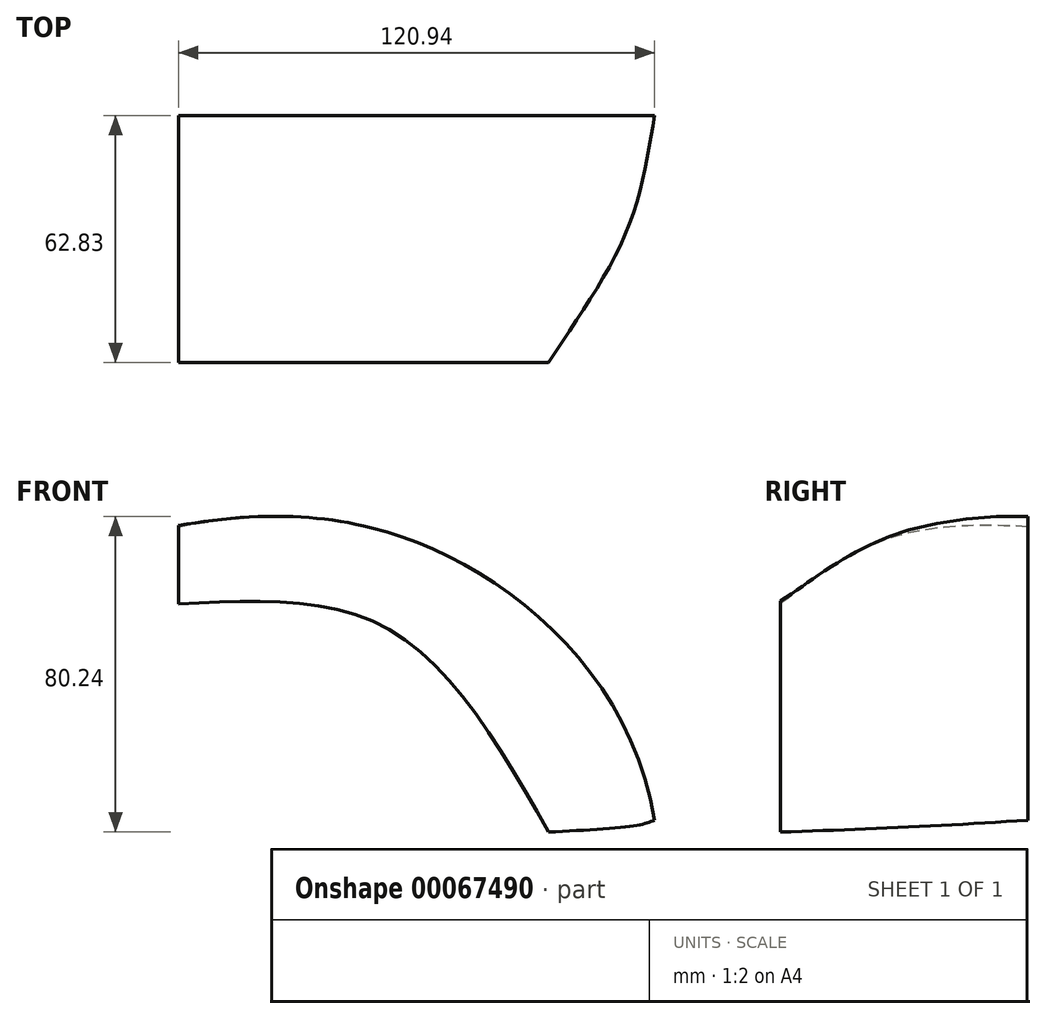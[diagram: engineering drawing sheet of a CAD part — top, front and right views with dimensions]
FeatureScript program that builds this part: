
annotation { "Feature Type Name" : "Feature", "Feature Type Description" : "" }
export const myFeature = defineFeature(function(context is Context, id is Id, definition is map)
    precondition{}
    {
        {
            var Q0;
            Q0=qCreatedBy(makeId("Right.planeOp"),FACE);
            cPlane(context, id + "F0", {"entities" : qUnion([Q0]), "cplaneType" : CPlaneType.OFFSET, "offset" : 140 * mm, "oppositeDirection" : true, "width" : 150 * mm, "height" : 150 * mm});
        }
        {
            var Q0;
            Q0=qCreatedBy(makeId("Right.planeOp"),FACE);
            cPlane(context, id + "F1", {"entities" : qUnion([Q0]), "cplaneType" : CPlaneType.OFFSET, "offset" : 95 * mm, "width" : 150 * mm, "height" : 150 * mm});
        }
        {
            var Q0;
            Q0=qCreatedBy(makeId("Front.planeOp"),FACE);
            var sketch = newSketch(context, id + "F2", { "sketchPlane" : qUnion([Q0])});
            skFitSpline(sketch, "E0", {"points": [v(-26.82, 108.95) * mm, v(37.57, 103.37) * mm, v(94.12, 34.37) * mm], "startDerivative": vector(145.94, 27.93) * mm, "endDerivative": vector(31.71, -191.73) * mm});
            skSolve(sketch);
        }
        {
            var Q0;
            Q0=qCreatedBy(makeId("Right.planeOp"),FACE);
            var Q1;
            Q1=sQuery(id+"F2.wireOp",VERTEX,"E0.start");
            cPlane(context, id + "F3", {"entities" : qUnion([Q0, Q1]), "cplaneType" : CPlaneType.PLANE_POINT, "offset" : 150 * mm, "width" : 150 * mm, "height" : 150 * mm});
        }
        {
            var Q0;
            Q0=qCreatedBy(id+"F1.planeOp",FACE);
            var sketch = newSketch(context, id + "F4", { "sketchPlane" : qUnion([Q0])});
            skFitSpline(sketch, "E1", {"points": [v(0, 34.37) * mm, v(-31.84, 34.05) * mm, v(-62.83, 29.9) * mm], "startDerivative": vector(-57.92, 0.78) * mm, "endDerivative": vector(-51.96, -19.36) * mm, "construction": true});
            skSolve(sketch);
        }
        {
            var Q0;
            Q0=sQuery(id+"F4.wireOp",VERTEX,"E1.end");
            var Q1;
            Q1=qCreatedBy(makeId("Front.planeOp"),FACE);
            cPlane(context, id + "F5", {"entities" : qUnion([Q0, Q1]), "cplaneType" : CPlaneType.PLANE_POINT, "offset" : 150 * mm, "width" : 150 * mm, "height" : 150 * mm});
        }
        {
            var Q0;
            Q0=qCreatedBy(id+"F3.planeOp",FACE);
            var sketch = newSketch(context, id + "F6", { "sketchPlane" : qUnion([Q0])});
            skFitSpline(sketch, "E2", {"points": [v(0, 108.95) * mm, v(-35.58, 105.84) * mm, v(-62.83, 89.32) * mm], "startDerivative": vector(-69.41, 3.44) * mm, "endDerivative": vector(-44.67, -35.7) * mm});
            skSolve(sketch);
        }
        {
            var Q0;
            Q0=qCreatedBy(id+"F5.planeOp",FACE);
            var sketch = newSketch(context, id + "F7", { "sketchPlane" : qUnion([Q0])});
            skFitSpline(sketch, "E3", {"points": [v(-26.82, 89.32) * mm, v(26.33, 83.05) * mm, v(67.21, 31.37) * mm], "startDerivative": vector(119.97, 6.53) * mm, "endDerivative": vector(68.67, -120.47) * mm});
            skSolve(sketch);
        }
        {
            var Q0;
            Q0=sQuery(id+"F7.wireOp",VERTEX,"E3.end");
            var Q1;
            Q1=sQuery(id+"F4.wireOp",VERTEX,"E1.2.internal");
            var Q2;
            Q2=sQuery(id+"F2.wireOp",VERTEX,"E0.end");
            cPlane(context, id + "F8", {"entities" : qUnion([Q0, Q1, Q2]), "cplaneType" : CPlaneType.THREE_POINT, "offset" : 150 * mm, "width" : 150 * mm, "height" : 150 * mm});
        }
        {
            var Q0;
            Q0=qCreatedBy(id+"F8.planeOp",FACE);
            var sketch = newSketch(context, id + "F9", { "sketchPlane" : qUnion([Q0])});
            skFitSpline(sketch, "E4", {"points": [v(65.23, 60.47) * mm, v(84.85, 27.58) * mm, v(92.18, -2.42) * mm], "startDerivative": vector(39.83, -62.1) * mm, "endDerivative": vector(10.39, -62.06) * mm});
            skSolve(sketch);
        }
        {
            var Q0;
            Q0=sQuery(id+"F6.wireOp",EDGE,"E2");
            var Q1;
            Q1=sQuery(id+"F9.wireOp",EDGE,"E4");
            var Q2;
            Q2=sQuery(id+"F2.wireOp",EDGE,"E0");
            var Q3;
            Q3=sQuery(id+"F7.wireOp",EDGE,"E3");
            loft(context, id + "F10", {"bodyType" : ToolBodyType.SURFACE, "addGuides" : true, "wireProfilesArray" : [{ "wireProfileEntities" : qUnion([Q0]) }, { "wireProfileEntities" : qUnion([Q1]) }], "guidesArray" : [{ "guideEntities" : qUnion([Q2]), "guideDerivativeType" : LoftGuideDerivativeType.DEFAULT, "guideDerivativeMagnitude" : 1 }, { "guideEntities" : qUnion([Q3]), "guideDerivativeType" : LoftGuideDerivativeType.DEFAULT, "guideDerivativeMagnitude" : 1 }]});
        }
    });
